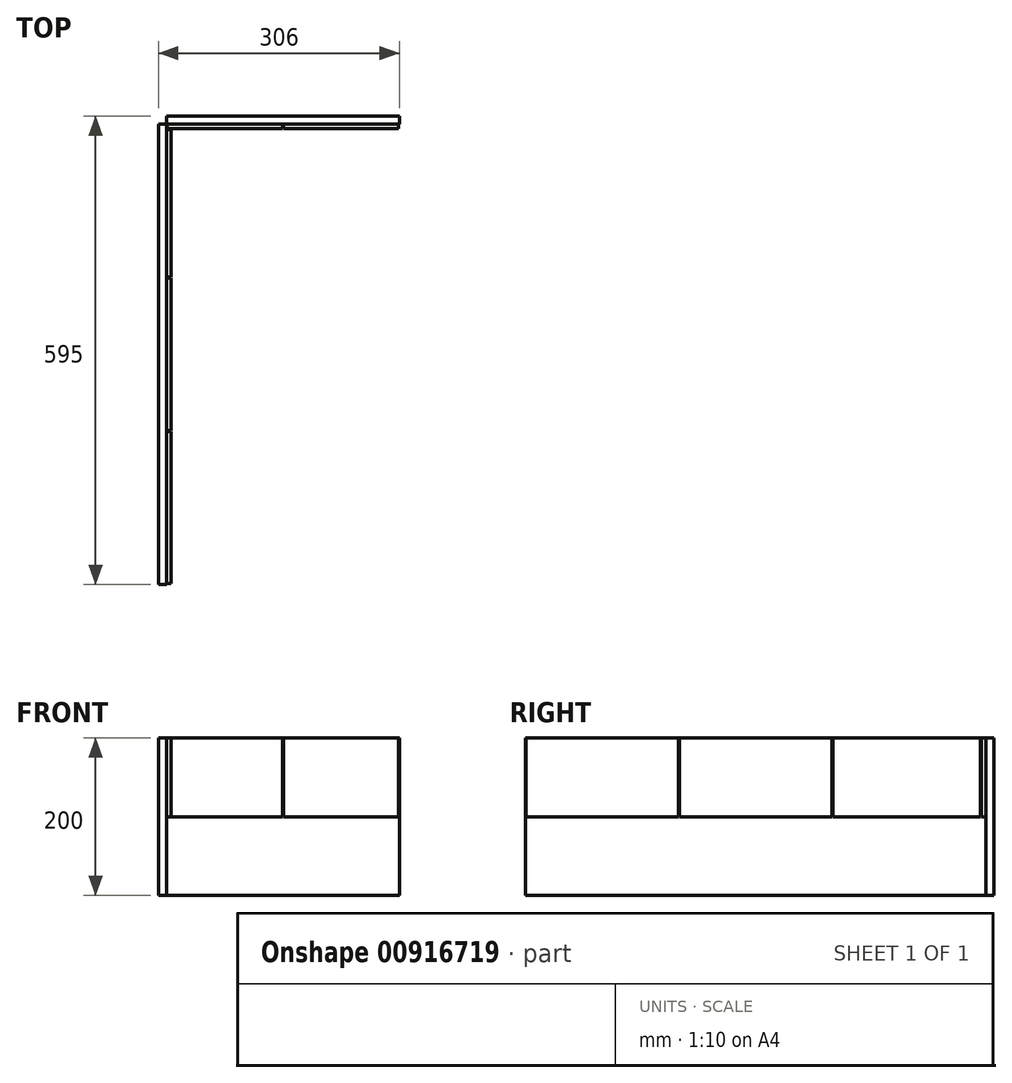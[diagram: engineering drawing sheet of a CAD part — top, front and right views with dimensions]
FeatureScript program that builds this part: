
annotation { "Feature Type Name" : "Feature", "Feature Type Description" : "" }
export const myFeature = defineFeature(function(context is Context, id is Id, definition is map)
    precondition{}
    {
        {
            var Q0;
            Q0=qCreatedBy(makeId("Top.planeOp"),FACE);
            var sketch = newSketch(context, id + "F0", { "sketchPlane" : qUnion([Q0])});
            skLineSegment(sketch, "E0.bottom", {"start": v(-64.68, 275.15) * mm, "end": v(-54.68, 275.15) * mm});
            skLineSegment(sketch, "E0.top", {"start": v(-64.68, -309.85) * mm, "end": v(-54.68, -309.85) * mm});
            skLineSegment(sketch, "E0.left", {"start": v(-64.68, 275.15) * mm, "end": v(-64.68, -309.85) * mm});
            skLineSegment(sketch, "E0.right", {"start": v(-54.68, 275.15) * mm, "end": v(-54.68, -309.85) * mm});
            skLineSegment(sketch, "E1.bottom", {"start": v(-54.68, 275.15) * mm, "end": v(241.32, 275.15) * mm});
            skLineSegment(sketch, "E1.top", {"start": v(-54.68, 285.15) * mm, "end": v(241.32, 285.15) * mm});
            skLineSegment(sketch, "E1.left", {"start": v(-54.68, 275.15) * mm, "end": v(-54.68, 285.15) * mm});
            skLineSegment(sketch, "E1.right", {"start": v(241.32, 275.15) * mm, "end": v(241.32, 285.15) * mm});
            skSolve(sketch);
        }
        {
            var Q0;
            Q0=makeQuery(id+"F0.imprint","IMPRINT",FACE,{"disambiguationData":[TD([[makeQuery(id+"F0.imprint","IMPRINT",EDGE,{"derivedFrom":sQuery(id+"F0.wireOp",EDGE,"E1.bottom")}),1.0]])]});
            var Q1;
            Q1=makeQuery(id+"F0.imprint","IMPRINT",FACE,{"disambiguationData":[TD([[makeQuery(id+"F0.imprint","IMPRINT",EDGE,{"derivedFrom":sQuery(id+"F0.wireOp",EDGE,"E0.bottom")}),-1.0]])]});
            extrude(context, id + "F1", {"entities" : qUnion([Q0, Q1]), "depth" : 200 * mm, "offsetDistance" : 25 * mm});
        }
        {
            var Q0;
            Q0=makeQuery(id+"F1.opExtrude","CAP_FACE",FACE,{"disambiguationData":[OSD([sQuery(id+"F0.wireOp",EDGE,"E1.bottom"),sQuery(id+"F0.wireOp",EDGE,"E1.top"),sQuery(id+"F0.wireOp",EDGE,"E1.left"),sQuery(id+"F0.wireOp",EDGE,"E1.right")])],"isStart":false});
            var sketch = newSketch(context, id + "F2", { "sketchPlane" : qUnion([Q0])});
            skLineSegment(sketch, "E2.bottom", {"start": v(-53.68, 275.15) * mm, "end": v(92.82, 275.15) * mm});
            skLineSegment(sketch, "E2.top", {"start": v(-53.68, 269.15) * mm, "end": v(92.82, 269.15) * mm});
            skLineSegment(sketch, "E2.left", {"start": v(-53.68, 275.15) * mm, "end": v(-53.68, 269.15) * mm});
            skLineSegment(sketch, "E2.right", {"start": v(92.82, 275.15) * mm, "end": v(92.82, 269.15) * mm});
            skLineSegment(sketch, "E3.bottom", {"start": v(93.82, 275.15) * mm, "end": v(240.32, 275.15) * mm});
            skLineSegment(sketch, "E3.top", {"start": v(93.82, 269.15) * mm, "end": v(240.32, 269.15) * mm});
            skLineSegment(sketch, "E3.left", {"start": v(93.82, 275.15) * mm, "end": v(93.82, 269.15) * mm});
            skLineSegment(sketch, "E3.right", {"start": v(240.32, 275.15) * mm, "end": v(240.32, 269.15) * mm});
            skSolve(sketch);
        }
        {
            var Q0;
            Q0=makeQuery(id+"F1.opExtrude","CAP_FACE",FACE,{"disambiguationData":[OSD([sQuery(id+"F0.wireOp",EDGE,"E0.bottom"),sQuery(id+"F0.wireOp",EDGE,"E0.top"),sQuery(id+"F0.wireOp",EDGE,"E0.left"),sQuery(id+"F0.wireOp",EDGE,"E0.right")])],"isStart":false});
            var sketch = newSketch(context, id + "F3", { "sketchPlane" : qUnion([Q0])});
            skLineSegment(sketch, "E4", {"start": v(-141.15, -114.85) * mm, "end": v(19.6, -114.85) * mm, "construction": true});
            skLineSegment(sketch, "E5", {"start": v(-141.15, 80.15) * mm, "end": v(19.6, 80.15) * mm, "construction": true});
            skLineSegment(sketch, "E6", {"start": v(-141.15, 315.15) * mm, "end": v(19.6, 315.15) * mm, "construction": true});
            skLineSegment(sketch, "E7", {"start": v(-64.68, 275.15) * mm, "end": v(-254.4, 275.15) * mm, "construction": true});
            skLineSegment(sketch, "E8", {"start": v(-54.68, 275.15) * mm, "end": v(-54.68, 295.8) * mm, "construction": true});
            skLineSegment(sketch, "E9", {"start": v(241.32, 272.62) * mm, "end": v(241.32, 338.37) * mm, "construction": true});
            skLineSegment(sketch, "E10.bottom", {"start": v(-54.68, -308.85) * mm, "end": v(-48.68, -308.85) * mm});
            skLineSegment(sketch, "E10.top", {"start": v(-54.68, -115.35) * mm, "end": v(-48.68, -115.35) * mm});
            skLineSegment(sketch, "E10.left", {"start": v(-54.68, -308.85) * mm, "end": v(-54.68, -115.35) * mm});
            skLineSegment(sketch, "E10.right", {"start": v(-48.68, -308.85) * mm, "end": v(-48.68, -115.35) * mm});
            skLineSegment(sketch, "E11.bottom", {"start": v(-54.68, -114.35) * mm, "end": v(-48.68, -114.35) * mm});
            skLineSegment(sketch, "E11.top", {"start": v(-54.68, 79.65) * mm, "end": v(-48.68, 79.65) * mm});
            skLineSegment(sketch, "E11.left", {"start": v(-54.68, -114.35) * mm, "end": v(-54.68, 79.65) * mm});
            skLineSegment(sketch, "E11.right", {"start": v(-48.68, -114.35) * mm, "end": v(-48.68, 79.65) * mm});
            skLineSegment(sketch, "E12.bottom", {"start": v(-54.68, 80.65) * mm, "end": v(-48.68, 80.65) * mm});
            skLineSegment(sketch, "E12.top", {"start": v(-54.68, 268.15) * mm, "end": v(-48.68, 268.15) * mm});
            skLineSegment(sketch, "E12.left", {"start": v(-54.68, 80.65) * mm, "end": v(-54.68, 268.15) * mm});
            skLineSegment(sketch, "E12.right", {"start": v(-48.68, 80.65) * mm, "end": v(-48.68, 268.15) * mm});
            skSolve(sketch);
        }
        {
            var Q0;
            Q0=makeQuery(id+"F3.imprint","IMPRINT",FACE,{"disambiguationData":[TD([[makeQuery(id+"F3.imprint","IMPRINT",EDGE,{"derivedFrom":sQuery(id+"F3.wireOp",EDGE,"E12.bottom")}),1.0]])]});
            var Q1;
            Q1=makeQuery(id+"F2.imprint","IMPRINT",FACE,{"disambiguationData":[TD([[makeQuery(id+"F2.imprint","IMPRINT",EDGE,{"derivedFrom":sQuery(id+"F2.wireOp",EDGE,"E2.bottom")}),-1.0]])]});
            var Q2;
            Q2=makeQuery(id+"F2.imprint","IMPRINT",FACE,{"disambiguationData":[TD([[makeQuery(id+"F2.imprint","IMPRINT",EDGE,{"derivedFrom":sQuery(id+"F2.wireOp",EDGE,"E3.bottom")}),-1.0]])]});
            var Q3;
            Q3=makeQuery(id+"F3.imprint","IMPRINT",FACE,{"disambiguationData":[TD([[makeQuery(id+"F3.imprint","IMPRINT",EDGE,{"derivedFrom":sQuery(id+"F3.wireOp",EDGE,"E11.bottom")}),1.0]])]});
            var Q4;
            Q4=makeQuery(id+"F3.imprint","IMPRINT",FACE,{"disambiguationData":[TD([[makeQuery(id+"F3.imprint","IMPRINT",EDGE,{"derivedFrom":sQuery(id+"F3.wireOp",EDGE,"E10.bottom")}),1.0]])]});
            extrude(context, id + "F4", {"entities" : qUnion([Q0, Q1, Q2, Q3, Q4]), "oppositeDirection" : true, "depth" : 100 * mm, "offsetDistance" : 25 * mm});
        }
    });
